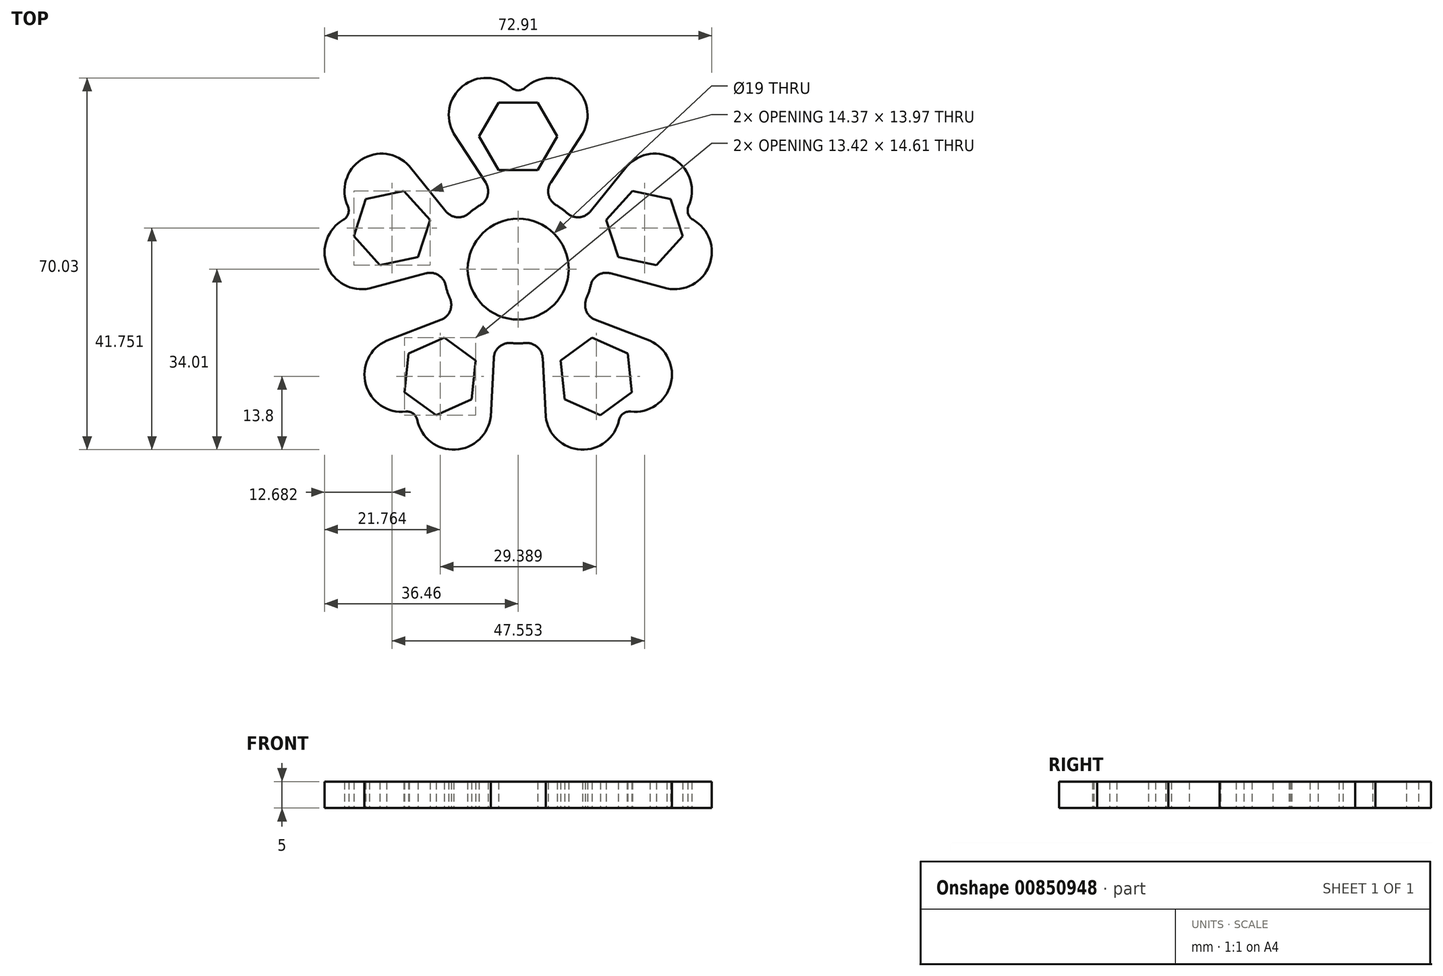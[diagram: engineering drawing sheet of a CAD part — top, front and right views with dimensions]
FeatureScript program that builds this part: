
annotation { "Feature Type Name" : "Feature", "Feature Type Description" : "" }
export const myFeature = defineFeature(function(context is Context, id is Id, definition is map)
    precondition{}
    {
        {
            var Q0;
            Q0=qCreatedBy(makeId("Top.planeOp"),FACE);
            var sketch = newSketch(context, id + "F0", { "sketchPlane" : qUnion([Q0])});
            skLineSegment(sketch, "E0", {"start": v(6.13, 16.29) * mm, "end": v(12.12, 25.52) * mm});
            skArc(sketch, "E1", {"start": v(12.12, 25.52) * mm, "mid": v(10.45, 34.47) * mm, "end": v(1.35, 34.19) * mm});
            skLineSegment(sketch, "E2.trimOffspring", {"start": v(0, 32.52) * mm, "end": v(0, 67.12) * mm, "construction": true});
            skLineSegment(sketch, "E3.trimOffspring", {"start": v(0, 19.02) * mm, "end": v(0, 41.02) * mm, "construction": true});
            skArc(sketch, "E4.MirrorCS", {"start": v(-12.13, 25.52) * mm, "mid": v(-10.45, 34.47) * mm, "end": v(-1.35, 34.19) * mm});
            skPoint(sketch, "E5.visualSharp", {"position": v(0, 32.52) * mm});
            skArc(sketch, "E5.filletArc", {"start": v(-1.35, 34.19) * mm, "mid": v(0, 33.67) * mm, "end": v(1.35, 34.19) * mm});
            skCircle(sketch, "E6.cCircle", {"center": v(0, 25.02) * mm, "radius": 6.36 * mm, "construction": true});
            skLineSegment(sketch, "E6.0", {"start": v(-3.67, 31.38) * mm, "end": v(3.67, 31.38) * mm});
            skLineSegment(sketch, "E6.1", {"start": v(3.67, 31.38) * mm, "end": v(7.34, 25.02) * mm});
            skLineSegment(sketch, "E6.2", {"start": v(7.34, 25.02) * mm, "end": v(3.67, 18.66) * mm});
            skLineSegment(sketch, "E6.3", {"start": v(3.67, 18.66) * mm, "end": v(-3.67, 18.66) * mm});
            skLineSegment(sketch, "E6.4", {"start": v(-3.67, 18.66) * mm, "end": v(-7.35, 25.02) * mm});
            skLineSegment(sketch, "E6.5", {"start": v(-7.35, 25.02) * mm, "end": v(-3.67, 31.38) * mm});
            skPoint(sketch, "E6.0.midPoint", {"position": v(0, 31.38) * mm});
            skCircle(sketch, "E7.0", {"center": v(0, 0.02) * mm, "radius": 14 * mm});
            skArc(sketch, "E8", {"start": v(6.13, 16.29) * mm, "mid": v(5.72, 13.97) * mm, "end": v(7.12, 12.07) * mm});
            skPoint(sketch, "E9.orphan", {"position": v(1.19, 8.67) * mm});
            skPoint(sketch, "E10.orphan", {"position": v(-1.19, 8.67) * mm});
            skArc(sketch, "E11.MirrorCS", {"start": v(-6.13, 16.29) * mm, "mid": v(-5.73, 13.97) * mm, "end": v(-7.12, 12.07) * mm});
            skLineSegment(sketch, "E12", {"start": v(-6.13, 16.29) * mm, "end": v(-12.13, 25.52) * mm});
            skLineSegment(sketch, "E13.1.0", {"start": v(-21.5, 14.73) * mm, "end": v(-16.6, 9.27) * mm});
            skPoint(sketch, "E13.1.1", {"position": v(-30.91, 10.06) * mm});
            skPoint(sketch, "E13.1.2", {"position": v(-29.83, 9.7) * mm});
            skPoint(sketch, "E13.1.3", {"position": v(-7.87, 3.82) * mm});
            skArc(sketch, "E13.1.4", {"start": v(-20.5, 19.43) * mm, "mid": v(-29.54, 20.6) * mm, "end": v(-32.09, 11.86) * mm});
            skCircle(sketch, "E13.1.5", {"center": v(-23.78, 7.74) * mm, "radius": 6.36 * mm, "construction": true});
            skArc(sketch, "E13.1.6", {"start": v(-13.58, 10.87) * mm, "mid": v(-11.5, 9.77) * mm, "end": v(-9.26, 10.51) * mm});
            skLineSegment(sketch, "E13.1.7", {"start": v(-17.37, -0.79) * mm, "end": v(-28, -3.64) * mm});
            skLineSegment(sketch, "E13.1.8", {"start": v(-18.07, 5.89) * mm, "end": v(-39, 12.69) * mm, "construction": true});
            skLineSegment(sketch, "E13.1.9", {"start": v(-18.86, 2.28) * mm, "end": v(-26.05, 0.76) * mm});
            skLineSegment(sketch, "E13.1.10", {"start": v(-28.7, 13.2) * mm, "end": v(-21.5, 14.73) * mm});
            skArc(sketch, "E13.1.11", {"start": v(-28, -3.64) * mm, "mid": v(-36, 0.72) * mm, "end": v(-32.92, 9.3) * mm});
            skLineSegment(sketch, "E13.1.12", {"start": v(-13.58, 10.87) * mm, "end": v(-20.5, 19.43) * mm});
            skLineSegment(sketch, "E13.1.13", {"start": v(-26.05, 0.76) * mm, "end": v(-30.96, 6.21) * mm});
            skPoint(sketch, "E13.1.14", {"position": v(-8.6, 1.56) * mm});
            skLineSegment(sketch, "E13.1.15", {"start": v(-16.6, 9.27) * mm, "end": v(-18.86, 2.28) * mm});
            skArc(sketch, "E13.1.16", {"start": v(-17.37, -0.79) * mm, "mid": v(-15.04, -1.12) * mm, "end": v(-13.67, -3.03) * mm});
            skArc(sketch, "E13.1.17", {"start": v(-32.92, 9.3) * mm, "mid": v(-32, 10.41) * mm, "end": v(-32.09, 11.86) * mm});
            skLineSegment(sketch, "E13.1.18", {"start": v(-30.96, 6.21) * mm, "end": v(-28.7, 13.2) * mm});
            skLineSegment(sketch, "E13.2.0", {"start": v(-20.64, -15.9) * mm, "end": v(-13.93, -12.9) * mm});
            skPoint(sketch, "E13.2.1", {"position": v(-19.1, -26.28) * mm});
            skPoint(sketch, "E13.2.2", {"position": v(-18.43, -25.36) * mm});
            skPoint(sketch, "E13.2.3", {"position": v(-6.05, -6.3) * mm});
            skArc(sketch, "E13.2.4", {"start": v(-24.8, -13.49) * mm, "mid": v(-28.7, -21.71) * mm, "end": v(-21.18, -26.84) * mm});
            skCircle(sketch, "E13.2.5", {"center": v(-14.7, -20.2) * mm, "radius": 6.36 * mm, "construction": true});
            skArc(sketch, "E13.2.6", {"start": v(-14.52, -9.54) * mm, "mid": v(-12.83, -7.9) * mm, "end": v(-12.85, -5.55) * mm});
            skLineSegment(sketch, "E13.2.7", {"start": v(-4.6, -16.75) * mm, "end": v(-5.18, -27.74) * mm});
            skLineSegment(sketch, "E13.2.8", {"start": v(-11.17, -15.36) * mm, "end": v(-24.1, -33.15) * mm, "construction": true});
            skLineSegment(sketch, "E13.2.9", {"start": v(-7.99, -17.22) * mm, "end": v(-8.75, -24.53) * mm});
            skLineSegment(sketch, "E13.2.10", {"start": v(-21.4, -23.2) * mm, "end": v(-20.64, -15.9) * mm});
            skArc(sketch, "E13.2.11", {"start": v(-5.18, -27.74) * mm, "mid": v(-11.8, -34) * mm, "end": v(-19, -28.42) * mm});
            skLineSegment(sketch, "E13.2.12", {"start": v(-14.52, -9.54) * mm, "end": v(-24.8, -13.49) * mm});
            skLineSegment(sketch, "E13.2.13", {"start": v(-8.75, -24.53) * mm, "end": v(-15.46, -27.51) * mm});
            skPoint(sketch, "E13.2.14", {"position": v(-4.13, -7.69) * mm});
            skLineSegment(sketch, "E13.2.15", {"start": v(-13.93, -12.9) * mm, "end": v(-7.99, -17.22) * mm});
            skArc(sketch, "E13.2.16", {"start": v(-4.6, -16.75) * mm, "mid": v(-3.57, -14.64) * mm, "end": v(-1.33, -13.92) * mm});
            skArc(sketch, "E13.2.17", {"start": v(-19, -28.42) * mm, "mid": v(-19.78, -27.2) * mm, "end": v(-21.18, -26.84) * mm});
            skLineSegment(sketch, "E13.2.18", {"start": v(-15.46, -27.51) * mm, "end": v(-21.4, -23.2) * mm});
            skCircle(sketch, "E14", {"center": v(0, 0) * mm, "radius": 9.5 * mm});
            skPoint(sketch, "E15.3.3.0", {"position": v(19.1, -26.28) * mm});
            skPoint(sketch, "E15.4.3.0", {"position": v(18.43, -25.36) * mm});
            skPoint(sketch, "E15.5.3.0", {"position": v(4.13, -7.69) * mm});
            skArc(sketch, "E15.6.3.0", {"start": v(5.18, -27.74) * mm, "mid": v(11.8, -34) * mm, "end": v(19, -28.42) * mm});
            skCircle(sketch, "E15.10.3.0", {"center": v(14.7, -20.2) * mm, "radius": 6.36 * mm, "construction": true});
            skArc(sketch, "E15.12.3.0", {"start": v(4.6, -16.75) * mm, "mid": v(3.57, -14.64) * mm, "end": v(1.32, -13.92) * mm});
            skLineSegment(sketch, "E15.16.3.0", {"start": v(14.52, -9.54) * mm, "end": v(24.8, -13.49) * mm});
            skLineSegment(sketch, "E15.19.3.0", {"start": v(11.17, -15.36) * mm, "end": v(24.1, -33.15) * mm, "construction": true});
            skLineSegment(sketch, "E15.22.3.0", {"start": v(13.93, -12.9) * mm, "end": v(20.63, -15.9) * mm});
            skLineSegment(sketch, "E15.25.3.0", {"start": v(15.46, -27.51) * mm, "end": v(8.75, -24.53) * mm});
            skArc(sketch, "E15.28.3.0", {"start": v(24.8, -13.49) * mm, "mid": v(28.7, -21.71) * mm, "end": v(21.18, -26.84) * mm});
            skLineSegment(sketch, "E15.32.3.0", {"start": v(4.6, -16.75) * mm, "end": v(5.18, -27.74) * mm});
            skLineSegment(sketch, "E15.35.3.0", {"start": v(20.63, -15.9) * mm, "end": v(21.4, -23.2) * mm});
            skPoint(sketch, "E15.38.3.0", {"position": v(6.05, -6.3) * mm});
            skLineSegment(sketch, "E15.39.3.0", {"start": v(7.98, -17.22) * mm, "end": v(13.93, -12.9) * mm});
            skArc(sketch, "E15.42.3.0", {"start": v(14.52, -9.54) * mm, "mid": v(12.83, -7.9) * mm, "end": v(12.84, -5.55) * mm});
            skLineSegment(sketch, "E15.45.3.0", {"start": v(8.75, -24.53) * mm, "end": v(7.98, -17.22) * mm});
            skArc(sketch, "E15.46.3.0", {"start": v(21.18, -26.84) * mm, "mid": v(19.78, -27.2) * mm, "end": v(19, -28.42) * mm});
            skLineSegment(sketch, "E15.50.3.0", {"start": v(21.4, -23.2) * mm, "end": v(15.46, -27.51) * mm});
            skPoint(sketch, "E16.3.4.0", {"position": v(30.9, 10.06) * mm});
            skPoint(sketch, "E16.4.4.0", {"position": v(29.82, 9.7) * mm});
            skPoint(sketch, "E16.5.4.0", {"position": v(8.6, 1.56) * mm});
            skArc(sketch, "E16.6.4.0", {"start": v(28, -3.64) * mm, "mid": v(36, 0.72) * mm, "end": v(32.92, 9.3) * mm});
            skCircle(sketch, "E16.10.4.0", {"center": v(23.78, 7.74) * mm, "radius": 6.36 * mm, "construction": true});
            skArc(sketch, "E16.12.4.0", {"start": v(17.37, -0.79) * mm, "mid": v(15.04, -1.12) * mm, "end": v(13.66, -3.03) * mm});
            skLineSegment(sketch, "E16.16.4.0", {"start": v(13.58, 10.87) * mm, "end": v(20.5, 19.43) * mm});
            skLineSegment(sketch, "E16.19.4.0", {"start": v(18.07, 5.89) * mm, "end": v(39, 12.69) * mm, "construction": true});
            skLineSegment(sketch, "E16.22.4.0", {"start": v(16.6, 9.27) * mm, "end": v(21.5, 14.73) * mm});
            skLineSegment(sketch, "E16.25.4.0", {"start": v(30.96, 6.21) * mm, "end": v(26.04, 0.76) * mm});
            skArc(sketch, "E16.28.4.0", {"start": v(20.5, 19.43) * mm, "mid": v(29.54, 20.6) * mm, "end": v(32.08, 11.86) * mm});
            skLineSegment(sketch, "E16.32.4.0", {"start": v(17.37, -0.79) * mm, "end": v(28, -3.64) * mm});
            skLineSegment(sketch, "E16.35.4.0", {"start": v(21.5, 14.73) * mm, "end": v(28.69, 13.2) * mm});
            skPoint(sketch, "E16.38.4.0", {"position": v(7.87, 3.82) * mm});
            skLineSegment(sketch, "E16.39.4.0", {"start": v(18.86, 2.28) * mm, "end": v(16.6, 9.27) * mm});
            skArc(sketch, "E16.42.4.0", {"start": v(13.58, 10.87) * mm, "mid": v(11.5, 9.77) * mm, "end": v(9.26, 10.51) * mm});
            skLineSegment(sketch, "E16.45.4.0", {"start": v(26.04, 0.76) * mm, "end": v(18.86, 2.28) * mm});
            skArc(sketch, "E16.46.4.0", {"start": v(32.08, 11.86) * mm, "mid": v(32, 10.41) * mm, "end": v(32.92, 9.3) * mm});
            skLineSegment(sketch, "E16.50.4.0", {"start": v(28.69, 13.2) * mm, "end": v(30.96, 6.21) * mm});
            skSolve(sketch);
        }
        {
            var Q0;
            Q0=makeQuery(id+"F0.imprint","IMPRINT",FACE,{"disambiguationData":[TD([[makeQuery(id+"F0.imprint","IMPRINT",EDGE,{"derivedFrom":sQuery(id+"F0.wireOp",EDGE,"E13.1.0")}),1.0]])]});
            var Q1;
            {var subQ0=sQuery(id+"F0.wireOp",EDGE,"E7.0");var subQ4=makeQuery(id+"F0.imprint","INTERSECT",VERTEX,{"derivedFrom":[subQ0,sQuery(id+"F0.wireOp",EDGE,"E8")]});Q1=makeQuery(id+"F0.imprint","IMPRINT",FACE,{"disambiguationData":[TD([[makeQuery(id+"F0.imprint","IMPRINT",EDGE,{"disambiguationData":[TD([[subQ4,1.0]])],"derivedFrom":subQ0}),1.0]])]});}
            var Q2;
            Q2=makeQuery(id+"F0.imprint","IMPRINT",FACE,{"disambiguationData":[TD([[makeQuery(id+"F0.imprint","IMPRINT",EDGE,{"derivedFrom":sQuery(id+"F0.wireOp",EDGE,"E13.2.0")}),1.0]])]});
            var Q3;
            Q3=makeQuery(id+"F0.imprint","IMPRINT",FACE,{"disambiguationData":[TD([[makeQuery(id+"F0.imprint","IMPRINT",EDGE,{"derivedFrom":sQuery(id+"F0.wireOp",EDGE,"E0")}),1.0]])]});
            var Q4;
            Q4=makeQuery(id+"F0.imprint","IMPRINT",FACE,{"disambiguationData":[TD([[makeQuery(id+"F0.imprint","IMPRINT",EDGE,{"derivedFrom":sQuery(id+"F0.wireOp",EDGE,"E15.6.4.0")}),1.0]])]});
            var Q5;
            Q5=makeQuery(id+"F0.imprint","IMPRINT",FACE,{"disambiguationData":[TD([[makeQuery(id+"F0.imprint","IMPRINT",EDGE,{"derivedFrom":sQuery(id+"F0.wireOp",EDGE,"E15.6.3.0")}),1.0]])]});
            var Q6;
            Q6=makeQuery(id+"F0.imprint","IMPRINT",FACE,{"disambiguationData":[TD([[makeQuery(id+"F0.imprint","IMPRINT",EDGE,{"derivedFrom":sQuery(id+"F0.wireOp",EDGE,"E16.6.4.0")}),1.0]])]});
            extrude(context, id + "F1", {"entities" : qUnion([Q0, Q1, Q2, Q3, Q4, Q5, Q6]), "depth" : 5 * mm, "offsetDistance" : 25 * mm});
        }
    });
